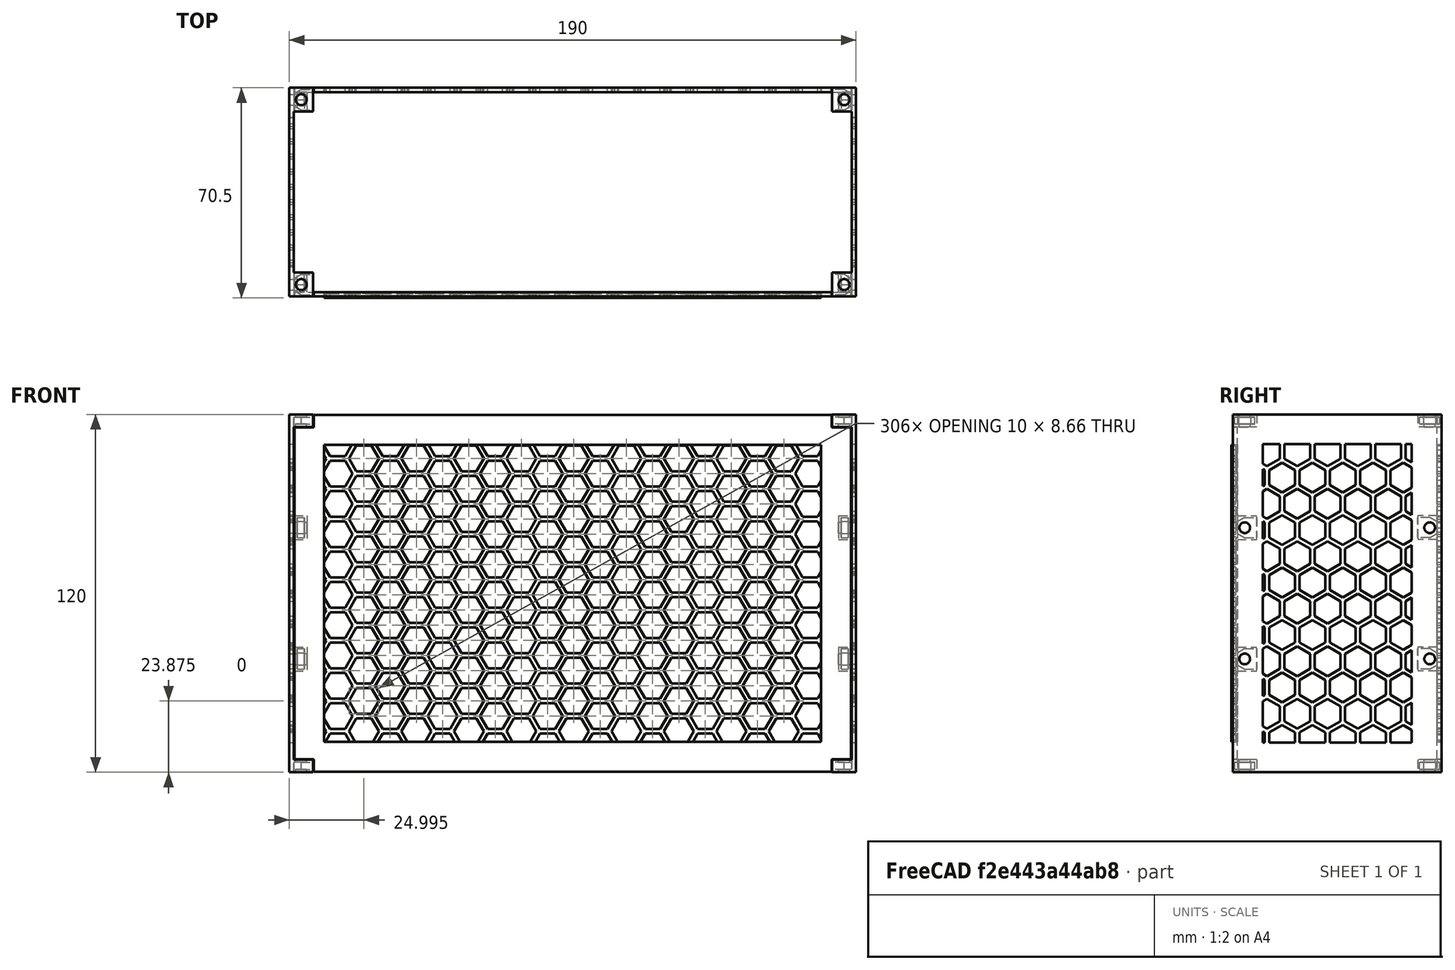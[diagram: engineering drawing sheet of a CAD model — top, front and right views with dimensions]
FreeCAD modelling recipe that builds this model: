
FCSTD DOCUMENT  (FreeCAD 0.18R4 (GitTag))
Label: tapasV3
License: CreativeCommons Attribution-ShareAlike
LicenseURL: http://creativecommons.org/licenses/by-sa/4.0/
objects: Part::Box×68, Part::Cut×60, Part::MultiFuse×46, Part::Cylinder×24, Part::Prism×16, Part::Feature×8
note: 222 computed .brp shape members not serialized (recipe doc carries the construction recipe); baked Part::Feature solids carry a one-line shape summary decoded from their .brp

FEATURE [Part::Feature] Cut001001001002003001008002002033001001001001001001001002001001002001045002003017008007002010007002014003017100  label="panal_simple_5_1.007"
  Placement = pos=(-89.5,0,0) rot=(0,1,0;1.5708rad)
  shape: bbox 1 x 260 x 260 mm, 5734 faces, 649 solids (baked)
FEATURE [Part::Feature] Cut001001001002003001008002002033001001001001001001001002001001002001045002003017008007002010007002014003017101  label="panal_simple_5_1.008"
  Placement = pos=(-88.5,0,0) rot=(0,1,0;1.5708rad)
  shape: bbox 1 x 260 x 260 mm, 5734 faces, 649 solids (baked)
FEATURE [Part::Feature] Cut001001001002003001008002002033001001001001001001001002001001002001045002003017008007002010007002014003017142  label="panal_simple_5_1.012"
  Placement = pos=(-113,18.7,0) rot=(-1,0,0;1.5708rad)
  shape: bbox 260 x 1 x 260 mm, 5734 faces, 649 solids (baked)
FEATURE [Part::Feature] Cut001001001002003001008002002033001001001001001001001002001001002001045002003017008007002010007002014003017075  label="panal_simple_5_1.006"
  Placement = pos=(-89.5,0,0) rot=(0,1,0;1.5708rad)
  shape: bbox 1 x 260 x 260 mm, 5734 faces, 649 solids (baked)
FEATURE [Part::Feature] Cut001001001002003001008002002033001001001001001001001002001001002001045002003017008007002010007002014003017148  label="panal_simple_5_1.013"
  Placement = pos=(-113,18.7,0) rot=(-1,0,0;1.5708rad)
  shape: bbox 260 x 1 x 260 mm, 5734 faces, 649 solids (baked)
FEATURE [Part::Feature] Cut001001001002003001008002002033001001001001001001001002001001002001045002003017008007002010007002014003017149  label="panal_simple_5_1.014"
  Placement = pos=(-113,17.8,0) rot=(-1,0,0;1.5708rad)
  shape: bbox 260 x 1 x 260 mm, 5734 faces, 649 solids (baked)
FEATURE [Part::Feature] Cut001004  label="panal_simple_5_1.5"
  Placement = pos=(-88.5,0,0) rot=(0,1,0;1.5708rad)
  shape: bbox 1 x 260 x 260 mm, 5734 faces, 649 solids (baked)
FEATURE [Part::Feature] Cut001001001002003001008002002033001001001001001001001002001001002001045002003017008007002010007002014003017141  label="panal_simple_5_1.011"
  Placement = pos=(-113,17.8,0) rot=(-1,0,0;1.5708rad)
  shape: bbox 260 x 1 x 260 mm, 5734 faces, 649 solids (baked)
FEATURE [Part::Box] Box089  label="Cube063"
  AttacherType = Attacher::AttachEngine3D
  Height = 4.2
  Length = 1
  Placement = pos=(-89,19,-111.2) rot=(0,0,1;0rad)
  Width = 8
FEATURE [Part::Box] Box079  label="Cube053"
  AttacherType = Attacher::AttachEngine3D
  Height = 100
  Length = 1.5
  Placement = pos=(-89,29,-217) rot=(0,0,1;0rad)
  Width = 50
FEATURE [Part::Box] Box077  label="Cube051"
  AttacherType = Attacher::AttachEngine3D
  Height = 120
  Length = 1.5
  Placement = pos=(-89,19,-227) rot=(0,0,1;0rad)
  Width = 70
FEATURE [Part::Cylinder] Cylinder037
  Angle = 360
  AttacherType = Attacher::AttachEngine3D
  Height = 10
  Placement = pos=(-91,85,-145) rot=(0.57735,0.57735,0.57735;2.0944rad)
  Radius = 1.8
FEATURE [Part::Cylinder] Cylinder035
  Angle = 360
  AttacherType = Attacher::AttachEngine3D
  Height = 10
  Placement = pos=(-91,23,-145) rot=(0.57735,0.57735,0.57735;2.0944rad)
  Radius = 1.8
FEATURE [Part::Cylinder] Cylinder038
  Angle = 360
  AttacherType = Attacher::AttachEngine3D
  Height = 10
  Placement = pos=(-91,85,-189) rot=(0.57735,0.57735,0.57735;2.0944rad)
  Radius = 1.8
FEATURE [Part::Box] Box078  label="Cube052"
  AttacherType = Attacher::AttachEngine3D
  Height = 100
  Length = 1.5
  Placement = pos=(-89,29,-217) rot=(0,0,1;0rad)
  Width = 50
FEATURE [Part::Cut] Cut001001001002003001008002002033001001001001001001001002001001002001045002003017008007002010007002014003017076
  Base = -> Box078
  Tool = -> Cut001004
FEATURE [Part::Cut] Cut001001001002003001008002002033001001001001001001001002001001002001045002003017008007002010007002014003017077  label="panal1"
  Base = -> Cut001001001002003001008002002033001001001001001001001002001001002001045002003017008007002010007002014003017076
  Tool = -> Cut001001001002003001008002002033001001001001001001001002001001002001045002003017008007002010007002014003017075
FEATURE [Part::Cylinder] Cylinder036
  Angle = 360
  AttacherType = Attacher::AttachEngine3D
  Height = 10
  Placement = pos=(-91,23,-189) rot=(0.57735,0.57735,0.57735;2.0944rad)
  Radius = 1.8
FEATURE [Part::Box] Box124  label="Cube098"
  AttacherType = Attacher::AttachEngine3D
  Height = 4.2
  Length = 1
  Placement = pos=(-89,19,-111.2) rot=(0,0,1;0rad)
  Width = 8
FEATURE [Part::Cylinder] Cylinder055
  Angle = 360
  AttacherType = Attacher::AttachEngine3D
  Height = 10
  Placement = pos=(-85,23,-112) rot=(0,0,1;0rad)
  Radius = 1.85
FEATURE [Part::Cylinder] Cylinder041
  Angle = 360
  AttacherType = Attacher::AttachEngine3D
  Height = 10
  Placement = pos=(-85,23,-112) rot=(0,0,1;0rad)
  Radius = 1.85
FEATURE [Part::Box] Box090  label="Cube064"
  AttacherType = Attacher::AttachEngine3D
  Height = 4.2
  Length = 7
  Placement = pos=(-88,19,-111.2) rot=(0,0,1;0rad)
  Width = 8
FEATURE [Part::Box] Box122  label="Cube096"
  AttacherType = Attacher::AttachEngine3D
  Height = 4.2
  Length = 1
  Placement = pos=(-89,19,-111.2) rot=(0,0,1;0rad)
  Width = 8
FEATURE [Part::Box] Box123  label="Cube097"
  AttacherType = Attacher::AttachEngine3D
  Height = 4.2
  Length = 7
  Placement = pos=(-88,19,-111.2) rot=(0,0,1;0rad)
  Width = 8
FEATURE [Part::Cut] Cut001001001002003001008002002033001001001001001001001002001001002001045002003017008007002010007002014003017118
  Base = -> Box123
  Tool = -> Cylinder055
FEATURE [Part::Box] Box088  label="Cube062"
  AttacherType = Attacher::AttachEngine3D
  Height = 2.4
  Length = 24
  Placement = pos=(-85,19.6,-110.2) rot=(0,0,1;0rad)
  Width = 6.8
FEATURE [Part::Prism] Prism014
  AttacherType = Attacher::AttachEngine3D
  Circumradius = 3.4
  Height = 2.4
  Placement = pos=(-85,23,-110.2) rot=(0,0,1;0.523599rad)
  Polygon = 6
FEATURE [Part::Prism] Prism013
  AttacherType = Attacher::AttachEngine3D
  Circumradius = 3.4
  Height = 2.4
  Placement = pos=(-85,23,-110.2) rot=(0,0,1;0.523599rad)
  Polygon = 6
FEATURE [Part::Box] Box086  label="Cube060"
  AttacherType = Attacher::AttachEngine3D
  Height = 4.2
  Length = 1
  Placement = pos=(-89,19,-111.2) rot=(0,0,1;0rad)
  Width = 8
FEATURE [Part::Prism] Prism015
  AttacherType = Attacher::AttachEngine3D
  Circumradius = 3.4
  Height = 2.4
  Placement = pos=(-85,23,-110.2) rot=(0,0,1;0.523599rad)
  Polygon = 6
FEATURE [Part::Box] Box087  label="Cube061"
  AttacherType = Attacher::AttachEngine3D
  Height = 4.2
  Length = 7
  Placement = pos=(-88,19,-111.2) rot=(0,0,1;0rad)
  Width = 8
FEATURE [Part::Cylinder] Cylinder039
  Angle = 360
  AttacherType = Attacher::AttachEngine3D
  Height = 10
  Placement = pos=(-85,23,-112) rot=(0,0,1;0rad)
  Radius = 1.85
FEATURE [Part::Box] Box085  label="Cube059"
  AttacherType = Attacher::AttachEngine3D
  Height = 2.4
  Length = 24
  Placement = pos=(-85,19.6,-110.2) rot=(0,0,1;0rad)
  Width = 6.8
FEATURE [Part::MultiFuse] Fusion007002009027003005008003003006005017002002002002002002002032016
  Placement = pos=(0,0,-0.1) rot=(0,0,1;0rad)
  Shapes = -> [Prism014,Box085]
FEATURE [Part::Box] Box082  label="Cube056"
  AttacherType = Attacher::AttachEngine3D
  Height = 2.4
  Length = 24
  Placement = pos=(-85,19.6,-110.2) rot=(0,0,1;0rad)
  Width = 6.8
FEATURE [Part::MultiFuse] Fusion007002009027003005008003003006005017002002002002002002002032014
  Placement = pos=(0,0,-0.1) rot=(0,0,1;0rad)
  Shapes = -> [Prism013,Box082]
FEATURE [Part::Box] Box083  label="Cube057"
  AttacherType = Attacher::AttachEngine3D
  Height = 4.2
  Length = 1
  Placement = pos=(-89,19,-111.2) rot=(0,0,1;0rad)
  Width = 8
FEATURE [Part::Box] Box084  label="Cube058"
  AttacherType = Attacher::AttachEngine3D
  Height = 4.2
  Length = 7
  Placement = pos=(-88,19,-111.2) rot=(0,0,1;0rad)
  Width = 8
FEATURE [Part::Cut] Cut001001001002003001008002002033001001001001001001001002001001002001045002003017008007002010007002014003017085
  Base = -> Box084
  Tool = -> Cylinder039
FEATURE [Part::MultiFuse] Fusion007002009027003005008003003006005017002002002002002002002032015
  Shapes = -> [Box083,Cut001001001002003001008002002033001001001001001001001002001001002001045002003017008007002010007002014003017085]
FEATURE [Part::Cut] Cut001001001002003001008002002033001001001001001001001002001001002001045002003017008007002010007002014003017084  label="pocket_v010"
  Base = -> Fusion007002009027003005008003003006005017002002002002002002002032015
  Tool = -> Fusion007002009027003005008003003006005017002002002002002002002032014
FEATURE [Part::Cylinder] Cylinder040
  Angle = 360
  AttacherType = Attacher::AttachEngine3D
  Height = 10
  Placement = pos=(-85,23,-112) rot=(0,0,1;0rad)
  Radius = 1.85
FEATURE [Part::Cut] Cut001001001002003001008002002033001001001001001001001002001001002001045002003017008007002010007002014003017087
  Base = -> Box087
  Tool = -> Cylinder040
FEATURE [Part::Box] Box104  label="Cube078"
  AttacherType = Attacher::AttachEngine3D
  Height = 4.2
  Length = 1
  Placement = pos=(-89,19,-111.2) rot=(0,0,1;0rad)
  Width = 8
FEATURE [Part::Box] Box125  label="Cube099"
  AttacherType = Attacher::AttachEngine3D
  Height = 4.2
  Length = 7
  Placement = pos=(-88,19,-111.2) rot=(0,0,1;0rad)
  Width = 8
FEATURE [Part::Box] Box121  label="Cube095"
  AttacherType = Attacher::AttachEngine3D
  Height = 2.4
  Length = 24
  Placement = pos=(-85,19.6,-110.2) rot=(0,0,1;0rad)
  Width = 6.8
FEATURE [Part::Box] Box112  label="Cube086"
  AttacherType = Attacher::AttachEngine3D
  Height = 4.2
  Length = 1
  Placement = pos=(-89,19,-111.2) rot=(0,0,1;0rad)
  Width = 8
FEATURE [Part::Box] Box111  label="Cube085"
  AttacherType = Attacher::AttachEngine3D
  Height = 2.4
  Length = 24
  Placement = pos=(-85,19.6,-110.2) rot=(0,0,1;0rad)
  Width = 6.8
FEATURE [Part::Cylinder] Cylinder052
  Angle = 360
  AttacherType = Attacher::AttachEngine3D
  Height = 10
  Placement = pos=(-85,23,-112) rot=(0,0,1;0rad)
  Radius = 1.85
FEATURE [Part::Box] Box117  label="Cube091"
  AttacherType = Attacher::AttachEngine3D
  Height = 4.2
  Length = 7
  Placement = pos=(-88,19,-111.2) rot=(0,0,1;0rad)
  Width = 8
FEATURE [Part::Cylinder] Cylinder048
  Angle = 360
  AttacherType = Attacher::AttachEngine3D
  Height = 10
  Placement = pos=(-91,23,-145) rot=(0.57735,0.57735,0.57735;2.0944rad)
  Radius = 1.8
FEATURE [Part::Cylinder] Cylinder050
  Angle = 360
  AttacherType = Attacher::AttachEngine3D
  Height = 10
  Placement = pos=(-91,23,-189) rot=(0.57735,0.57735,0.57735;2.0944rad)
  Radius = 1.8
FEATURE [Part::Cylinder] Cylinder054
  Angle = 360
  AttacherType = Attacher::AttachEngine3D
  Height = 10
  Placement = pos=(-85,23,-112) rot=(0,0,1;0rad)
  Radius = 1.85
FEATURE [Part::Prism] Prism023
  AttacherType = Attacher::AttachEngine3D
  Circumradius = 3.4
  Height = 2.4
  Placement = pos=(-85,23,-110.2) rot=(0,0,1;0.523599rad)
  Polygon = 6
FEATURE [Part::Cylinder] Cylinder053
  Angle = 360
  AttacherType = Attacher::AttachEngine3D
  Height = 10
  Placement = pos=(-85,23,-112) rot=(0,0,1;0rad)
  Radius = 1.85
FEATURE [Part::Prism] Prism025
  AttacherType = Attacher::AttachEngine3D
  Circumradius = 3.4
  Height = 2.4
  Placement = pos=(-85,23,-110.2) rot=(0,0,1;0.523599rad)
  Polygon = 6
FEATURE [Part::Box] Box115  label="Cube089"
  AttacherType = Attacher::AttachEngine3D
  Height = 2.4
  Length = 24
  Placement = pos=(-85,19.6,-110.2) rot=(0,0,1;0rad)
  Width = 6.8
FEATURE [Part::Box] Box113  label="Cube087"
  AttacherType = Attacher::AttachEngine3D
  Height = 4.2
  Length = 7
  Placement = pos=(-88,19,-111.2) rot=(0,0,1;0rad)
  Width = 8
FEATURE [Part::Cut] Cut001001001002003001008002002033001001001001001001001002001001002001045002003017008007002010007002014003017107
  Base = -> Box113
  Tool = -> Cylinder053
FEATURE [Part::Box] Box116  label="Cube090"
  AttacherType = Attacher::AttachEngine3D
  Height = 4.2
  Length = 1
  Placement = pos=(-89,19,-111.2) rot=(0,0,1;0rad)
  Width = 8
FEATURE [Part::Box] Box109  label="Cube083"
  AttacherType = Attacher::AttachEngine3D
  Height = 100
  Length = 1.5
  Placement = pos=(-89,29,-217) rot=(0,0,1;0rad)
  Width = 50
FEATURE [Part::Cut] Cut001001001002003001008002002033001001001001001001001002001001002001045002003017008007002010007002014003017111
  Base = -> Box109
  Tool = -> Cut001001001002003001008002002033001001001001001001001002001001002001045002003017008007002010007002014003017101
FEATURE [Part::Cylinder] Cylinder049
  Angle = 360
  AttacherType = Attacher::AttachEngine3D
  Height = 10
  Placement = pos=(-91,85,-189) rot=(0.57735,0.57735,0.57735;2.0944rad)
  Radius = 1.8
FEATURE [Part::Cylinder] Cylinder051
  Angle = 360
  AttacherType = Attacher::AttachEngine3D
  Height = 10
  Placement = pos=(-85,23,-112) rot=(0,0,1;0rad)
  Radius = 1.85
FEATURE [Part::Prism] Prism021
  AttacherType = Attacher::AttachEngine3D
  Circumradius = 3.4
  Height = 2.4
  Placement = pos=(-85,23,-110.2) rot=(0,0,1;0.523599rad)
  Polygon = 6
FEATURE [Part::Prism] Prism022
  AttacherType = Attacher::AttachEngine3D
  Circumradius = 3.4
  Height = 2.4
  Placement = pos=(-85,23,-110.2) rot=(0,0,1;0.523599rad)
  Polygon = 6
FEATURE [Part::Box] Box114  label="Cube088"
  AttacherType = Attacher::AttachEngine3D
  Height = 2.4
  Length = 24
  Placement = pos=(-85,19.6,-110.2) rot=(0,0,1;0rad)
  Width = 6.8
FEATURE [Part::Box] Box110  label="Cube084"
  AttacherType = Attacher::AttachEngine3D
  Height = 4.2
  Length = 7
  Placement = pos=(-88,19,-111.2) rot=(0,0,1;0rad)
  Width = 8
FEATURE [Part::Cut] Cut001001001002003001008002002033001001001001001001001002001001002001045002003017008007002010007002014003017114
  Base = -> Box110
  Tool = -> Cylinder051
FEATURE [Part::Box] Box118  label="Cube092"
  AttacherType = Attacher::AttachEngine3D
  Height = 4.2
  Length = 1
  Placement = pos=(-89,19,-111.2) rot=(0,0,1;0rad)
  Width = 8
FEATURE [Part::Prism] Prism024
  AttacherType = Attacher::AttachEngine3D
  Circumradius = 3.4
  Height = 2.4
  Placement = pos=(-85,23,-110.2) rot=(0,0,1;0.523599rad)
  Polygon = 6
FEATURE [Part::Box] Box119  label="Cube093"
  AttacherType = Attacher::AttachEngine3D
  Height = 2.4
  Length = 24
  Placement = pos=(-85,19.6,-110.2) rot=(0,0,1;0rad)
  Width = 6.8
FEATURE [Part::Box] Box120  label="Cube094"
  AttacherType = Attacher::AttachEngine3D
  Height = 4.2
  Length = 7
  Placement = pos=(-88,19,-111.2) rot=(0,0,1;0rad)
  Width = 8
FEATURE [Part::Cut] Cut001001001002003001008002002033001001001001001001001002001001002001045002003017008007002010007002014003017115
  Base = -> Box120
  Tool = -> Cylinder054
FEATURE [Part::MultiFuse] Fusion007002009027003005008003003006005017002002002002002002002032036
  Shapes = -> [Box118,Cut001001001002003001008002002033001001001001001001001002001001002001045002003017008007002010007002014003017115]
FEATURE [Part::MultiFuse] Fusion007002009027003005008003003006005017002002002002002002002032018
  Placement = pos=(0,0,-0.1) rot=(0,0,1;0rad)
  Shapes = -> [Prism015,Box088]
FEATURE [Part::MultiFuse] Fusion007002009027003005008003003006005017002002002002002002002032034
  Placement = pos=(0,0,-0.1) rot=(0,0,1;0rad)
  Shapes = -> [Prism021,Box114]
FEATURE [Part::MultiFuse] Fusion007002009027003005008003003006005017002002002002002002002032017
  Shapes = -> [Box086,Cut001001001002003001008002002033001001001001001001001002001001002001045002003017008007002010007002014003017087]
FEATURE [Part::Cut] Cut001001001002003001008002002033001001001001001001001002001001002001045002003017008007002010007002014003017086  label="pocket_v011"
  Base = -> Fusion007002009027003005008003003006005017002002002002002002002032017
  Placement = pos=(0,0,-115.8) rot=(0,0,1;0rad)
  Tool = -> Fusion007002009027003005008003003006005017002002002002002002002032016
FEATURE [Part::MultiFuse] Fusion007002009027003005008003003006005017002002002002002002002032035
  Placement = pos=(0,0,-0.1) rot=(0,0,1;0rad)
  Shapes = -> [Prism023,Box111]
FEATURE [Part::MultiFuse] Fusion007002009027003005008003003006005017002002002002002002002032032
  Placement = pos=(0,0,-0.1) rot=(0,0,1;0rad)
  Shapes = -> [Prism022,Box115]
FEATURE [Part::Cut] Cut001001001002003001008002002033001001001001001001001002001001002001045002003017008007002010007002014003017089
  Base = -> Box090
  Tool = -> Cylinder041
FEATURE [Part::MultiFuse] Fusion007002009027003005008003003006005017002002002002002002002032019
  Shapes = -> [Box089,Cut001001001002003001008002002033001001001001001001001002001001002001045002003017008007002010007002014003017089]
FEATURE [Part::Cut] Cut001001001002003001008002002033001001001001001001001002001001002001045002003017008007002010007002014003017088  label="pocket_v012"
  Base = -> Fusion007002009027003005008003003006005017002002002002002002002032019
  Placement = pos=(0,62,0) rot=(0,0,1;0rad)
  Tool = -> Fusion007002009027003005008003003006005017002002002002002002002032018
FEATURE [Part::Cylinder] Cylinder056
  Angle = 360
  AttacherType = Attacher::AttachEngine3D
  Height = 10
  Placement = pos=(-85,23,-112) rot=(0,0,1;0rad)
  Radius = 1.85
FEATURE [Part::Cut] Cut001001001002003001008002002033001001001001001001001002001001002001045002003017008007002010007002014003017119
  Base = -> Box125
  Tool = -> Cylinder056
FEATURE [Part::Prism] Prism020
  AttacherType = Attacher::AttachEngine3D
  Circumradius = 3.4
  Height = 2.4
  Placement = pos=(-85,23,-110.2) rot=(0,0,1;0.523599rad)
  Polygon = 6
FEATURE [Part::Cylinder] Cylinder047
  Angle = 360
  AttacherType = Attacher::AttachEngine3D
  Height = 10
  Placement = pos=(-91,85,-145) rot=(0.57735,0.57735,0.57735;2.0944rad)
  Radius = 1.8
FEATURE [Part::Box] Box103  label="Cube077"
  AttacherType = Attacher::AttachEngine3D
  Height = 2.4
  Length = 24
  Placement = pos=(-85,19.6,-110.2) rot=(0,0,1;0rad)
  Width = 6.8
FEATURE [Part::MultiFuse] Fusion007002009027003005008003003006005017002002002002002002002032028
  Placement = pos=(0,0,-0.1) rot=(0,0,1;0rad)
  Shapes = -> [Prism020,Box103]
FEATURE [Part::Box] Box106  label="Cube080"
  AttacherType = Attacher::AttachEngine3D
  Height = 4.2
  Length = 1
  Placement = pos=(-89,19,-111.2) rot=(0,0,1;0rad)
  Width = 8
FEATURE [Part::Cylinder] Cylinder046
  Angle = 360
  AttacherType = Attacher::AttachEngine3D
  Height = 10
  Placement = pos=(-85,23,-112) rot=(0,0,1;0rad)
  Radius = 1.85
FEATURE [Part::Box] Box107  label="Cube081"
  AttacherType = Attacher::AttachEngine3D
  Height = 100
  Length = 1.5
  Placement = pos=(-89,29,-217) rot=(0,0,1;0rad)
  Width = 50
FEATURE [Part::Box] Box108  label="Cube082"
  AttacherType = Attacher::AttachEngine3D
  Height = 120
  Length = 1.5
  Placement = pos=(-89,19,-227) rot=(0,0,1;0rad)
  Width = 70
FEATURE [Part::Box] Box105  label="Cube079"
  AttacherType = Attacher::AttachEngine3D
  Height = 4.2
  Length = 7
  Placement = pos=(-88,19,-111.2) rot=(0,0,1;0rad)
  Width = 8
FEATURE [Part::Cut] Cut001001001002003001008002002033001001001001001001001002001001002001045002003017008007002010007002014003017099
  Base = -> Box105
  Tool = -> Cylinder046
FEATURE [Part::MultiFuse] Fusion007002009027003005008003003006005017002002002002002002002032029
  Shapes = -> [Box104,Cut001001001002003001008002002033001001001001001001001002001001002001045002003017008007002010007002014003017099]
FEATURE [Part::Cut] Cut001001001002003001008002002033001001001001001001001002001001002001045002003017008007002010007002014003017098  label="pocket_v017"
  Base = -> Fusion007002009027003005008003003006005017002002002002002002002032029
  Placement = pos=(0,62,-115.8) rot=(0,0,1;0rad)
  Tool = -> Fusion007002009027003005008003003006005017002002002002002002002032028
FEATURE [Part::MultiFuse] Fusion007002009027003005008003003006005017002002002002002002002032006  label="lateral_izquierdo_v2_001"
  Shapes = -> [Box077,Cut001001001002003001008002002033001001001001001001001002001001002001045002003017008007002010007002014003017088,Cut001001001002003001008002002033001001001001001001001002001001002001045002003017008007002010007002014003017084,Cut001001001002003001008002002033001001001001001001001002001001002001045002003017008007002010007002014003017086,+1 more]
FEATURE [Part::Cut] Cut001001001002003001008002002033001001001001001001001002001001002001045002003017008007002010007002014003017078
  Base = -> Fusion007002009027003005008003003006005017002002002002002002002032006
  Tool = -> Box079
FEATURE [Part::MultiFuse] Fusion007002009027003005008003003006005017002002002002002002002032007  label="lateral_izquierdo_v2_00101"
  Shapes = -> [Cut001001001002003001008002002033001001001001001001001002001001002001045002003017008007002010007002014003017078,Cut001001001002003001008002002033001001001001001001001002001001002001045002003017008007002010007002014003017077]
FEATURE [Part::Cut] Cut001001001002003001008002002033001001001001001001001002001001002001045002003017008007002010007002014003017079
  Base = -> Fusion007002009027003005008003003006005017002002002002002002002032007
  Tool = -> Cylinder035
FEATURE [Part::Cut] Cut001001001002003001008002002033001001001001001001001002001001002001045002003017008007002010007002014003017080
  Base = -> Cut001001001002003001008002002033001001001001001001001002001001002001045002003017008007002010007002014003017079
  Tool = -> Cylinder036
FEATURE [Part::Cut] Cut001001001002003001008002002033001001001001001001001002001001002001045002003017008007002010007002014003017081
  Base = -> Cut001001001002003001008002002033001001001001001001001002001001002001045002003017008007002010007002014003017080
  Tool = -> Cylinder038
FEATURE [Part::Cut] Cut001001001002003001008002002033001001001001001001001002001001002001045002003017008007002010007002014003017082  label="lateral_izquierdo_v3"
  Base = -> Cut001001001002003001008002002033001001001001001001001002001001002001045002003017008007002010007002014003017081
  Tool = -> Cylinder037
FEATURE [Part::Cut] Cut001001001002003001008002002033001001001001001001001002001001002001045002003017008007002010007002014003017105
  Base = -> Box117
  Tool = -> Cylinder052
FEATURE [Part::MultiFuse] Fusion007002009027003005008003003006005017002002002002002002002032033
  Shapes = -> [Box116,Cut001001001002003001008002002033001001001001001001001002001001002001045002003017008007002010007002014003017105]
FEATURE [Part::Cut] Cut001001001002003001008002002033001001001001001001001002001001002001045002003017008007002010007002014003017104  label="pocket_v018"
  Base = -> Fusion007002009027003005008003003006005017002002002002002002002032033
  Placement = pos=(-176.5,46,0) rot=(0,0,1;3.14159rad)
  Tool = -> Fusion007002009027003005008003003006005017002002002002002002002032032
FEATURE [Part::Cut] Cut001001001002003001008002002033001001001001001001001002001001002001045002003017008007002010007002014003017103  label="panal002"
  Base = -> Cut001001001002003001008002002033001001001001001001001002001001002001045002003017008007002010007002014003017111
  Tool = -> Cut001001001002003001008002002033001001001001001001001002001001002001045002003017008007002010007002014003017100
FEATURE [Part::MultiFuse] Fusion007002009027003005008003003006005017002002002002002002002032038
  Shapes = -> [Box112,Cut001001001002003001008002002033001001001001001001001002001001002001045002003017008007002010007002014003017107]
FEATURE [Part::Cut] Cut001001001002003001008002002033001001001001001001001002001001002001045002003017008007002010007002014003017106  label="pocket_v019"
  Base = -> Fusion007002009027003005008003003006005017002002002002002002002032038
  Placement = pos=(-176.5,46,-115.8) rot=(0,0,1;3.14159rad)
  Tool = -> Fusion007002009027003005008003003006005017002002002002002002002032034
FEATURE [Part::MultiFuse] Fusion007002009027003005008003003006005017002002002002002002002032040
  Placement = pos=(0,0,-0.1) rot=(0,0,1;0rad)
  Shapes = -> [Prism025,Box121]
FEATURE [Part::MultiFuse] Fusion007002009027003005008003003006005017002002002002002002002032041
  Shapes = -> [Box122,Cut001001001002003001008002002033001001001001001001001002001001002001045002003017008007002010007002014003017118]
FEATURE [Part::Cut] Cut001001001002003001008002002033001001001001001001001002001001002001045002003017008007002010007002014003017117  label="pocket_v022"
  Base = -> Fusion007002009027003005008003003006005017002002002002002002002032041
  Placement = pos=(23.9,108,-168) rot=(0.57735,0.57735,0.57735;2.0944rad)
  Tool = -> Fusion007002009027003005008003003006005017002002002002002002002032040
FEATURE [Part::MultiFuse] Fusion007002009027003005008003003006005017002002002002002002002032037
  Shapes = -> [Box106,Cut001001001002003001008002002033001001001001001001001002001001002001045002003017008007002010007002014003017114]
FEATURE [Part::Cut] Cut001001001002003001008002002033001001001001001001001002001001002001045002003017008007002010007002014003017113  label="pocket_v020"
  Base = -> Fusion007002009027003005008003003006005017002002002002002002002032037
  Placement = pos=(-176.5,108,0) rot=(0,0,1;3.14159rad)
  Tool = -> Fusion007002009027003005008003003006005017002002002002002002002032035
FEATURE [Part::MultiFuse] Fusion007002009027003005008003003006005017002002002002002002002032039
  Placement = pos=(0,0,-0.1) rot=(0,0,1;0rad)
  Shapes = -> [Prism024,Box119]
FEATURE [Part::Cut] Cut001001001002003001008002002033001001001001001001001002001001002001045002003017008007002010007002014003017116  label="pocket_v021"
  Base = -> Fusion007002009027003005008003003006005017002002002002002002002032036
  Placement = pos=(-176.5,108,-115.8) rot=(0,0,1;3.14159rad)
  Tool = -> Fusion007002009027003005008003003006005017002002002002002002002032039
FEATURE [Part::MultiFuse] Fusion007002009027003005008003003006005017002002002002002002002032030  label="lateral_izquierdo_v2_00102"
  Shapes = -> [Box108,Cut001001001002003001008002002033001001001001001001001002001001002001045002003017008007002010007002014003017113,Cut001001001002003001008002002033001001001001001001001002001001002001045002003017008007002010007002014003017104,Cut001001001002003001008002002033001001001001001001001002001001002001045002003017008007002010007002014003017106,+1 more]
FEATURE [Part::Cut] Cut001001001002003001008002002033001001001001001001001002001001002001045002003017008007002010007002014003017108
  Base = -> Fusion007002009027003005008003003006005017002002002002002002002032030
  Tool = -> Box107
FEATURE [Part::MultiFuse] Fusion007002009027003005008003003006005017002002002002002002002032031  label="lateral_izquierdo_v2_00103"
  Shapes = -> [Cut001001001002003001008002002033001001001001001001001002001001002001045002003017008007002010007002014003017108,Cut001001001002003001008002002033001001001001001001001002001001002001045002003017008007002010007002014003017103]
FEATURE [Part::Cut] Cut001001001002003001008002002033001001001001001001001002001001002001045002003017008007002010007002014003017110
  Base = -> Fusion007002009027003005008003003006005017002002002002002002002032031
  Tool = -> Cylinder048
FEATURE [Part::Cut] Cut001001001002003001008002002033001001001001001001001002001001002001045002003017008007002010007002014003017109
  Base = -> Cut001001001002003001008002002033001001001001001001001002001001002001045002003017008007002010007002014003017110
  Tool = -> Cylinder050
FEATURE [Part::Cut] Cut001001001002003001008002002033001001001001001001001002001001002001045002003017008007002010007002014003017112
  Base = -> Cut001001001002003001008002002033001001001001001001001002001001002001045002003017008007002010007002014003017109
  Tool = -> Cylinder049
FEATURE [Part::Cut] Cut001001001002003001008002002033001001001001001001001002001001002001045002003017008007002010007002014003017102  label="lateral_derecho_v3"
  Base = -> Cut001001001002003001008002002033001001001001001001001002001001002001045002003017008007002010007002014003017112
  Placement = pos=(188.5,0,0) rot=(0,0,1;0rad)
  Tool = -> Cylinder047
FEATURE [Part::MultiFuse] Fusion007002009027003005008003003006005017002002002002002002002032043
  Shapes = -> [Box124,Cut001001001002003001008002002033001001001001001001001002001001002001045002003017008007002010007002014003017119]
FEATURE [Part::Box] Box156  label="Cube124"
  AttacherType = Attacher::AttachEngine3D
  Height = 4.4
  Length = 6.7
  Placement = pos=(92.8,17,-227) rot=(0,0,1;0rad)
  Width = 10
FEATURE [Part::Box] Box157  label="Cube125"
  AttacherType = Attacher::AttachEngine3D
  Height = 4.4
  Length = 6.7
  Placement = pos=(92.8,17,-111.4) rot=(0,0,1;0rad)
  Width = 10
FEATURE [Part::Box] Box152  label="base_tapa003"
  AttacherType = Attacher::AttachEngine3D
  Height = 99.6
  Length = 166.6
  Placement = pos=(-77.3,18.5,-216.8) rot=(0,0,1;0rad)
  Width = 1.5
FEATURE [Part::Cut] Cut001001001002003001008002002033001001001001001001001002001001002001045002003017008007002010007002014003017143
  Base = -> Box152
  Tool = -> Cut001001001002003001008002002033001001001001001001001002001001002001045002003017008007002010007002014003017142
FEATURE [Part::Cut] Cut001001001002003001008002002033001001001001001001001002001001002001045002003017008007002010007002014003017144  label="enrejillado_base_o_tapa"
  Base = -> Cut001001001002003001008002002033001001001001001001001002001001002001045002003017008007002010007002014003017143
  Placement = pos=(0,69,0) rot=(0,0,1;0rad)
  Tool = -> Cut001001001002003001008002002033001001001001001001001002001001002001045002003017008007002010007002014003017141
FEATURE [Part::Box] Box150  label="corta_enrejilaldo_base_tapa001"
  AttacherType = Attacher::AttachEngine3D
  Height = 99.6
  Length = 166.6
  Placement = pos=(-77.3,18.5,-216.8) rot=(0,0,1;0rad)
  Width = 3
FEATURE [Part::Box] Box153  label="base_tapa004"
  AttacherType = Attacher::AttachEngine3D
  Height = 99.6
  Length = 166.6
  Placement = pos=(-77.3,86.5,-216.8) rot=(0,0,1;0rad)
  Width = 3
FEATURE [Part::Box] Box154  label="base_tapa005"
  AttacherType = Attacher::AttachEngine3D
  Height = 99.6
  Length = 166.6
  Placement = pos=(-77.3,18.5,-216.8) rot=(0,0,1;0rad)
  Width = 1.5
FEATURE [Part::Cut] Cut001001001002003001008002002033001001001001001001001002001001002001045002003017008007002010007002014003017147
  Base = -> Box154
  Tool = -> Cut001001001002003001008002002033001001001001001001001002001001002001045002003017008007002010007002014003017148
FEATURE [Part::Cut] Cut001001001002003001008002002033001001001001001001001002001001002001045002003017008007002010007002014003017155
  Base = -> Cut001001001002003001008002002033001001001001001001001002001001002001045002003017008007002010007002014003017147
  Tool = -> Cut001001001002003001008002002033001001001001001001001002001001002001045002003017008007002010007002014003017149
FEATURE [Part::Box] Box149  label="Cube122"
  AttacherType = Attacher::AttachEngine3D
  Height = 4.4
  Length = 6.7
  Placement = pos=(-87.5,17,-111.4) rot=(0,0,1;0rad)
  Width = 10
FEATURE [Part::Box] Box155  label="Cube123"
  AttacherType = Attacher::AttachEngine3D
  Height = 4.4
  Length = 6.7
  Placement = pos=(-87.5,17,-111.4) rot=(0,0,1;0rad)
  Width = 10
FEATURE [Part::Box] Box158  label="Cube126"
  AttacherType = Attacher::AttachEngine3D
  Height = 4.4
  Length = 6.7
  Placement = pos=(-87.5,17,-227) rot=(0,0,1;0rad)
  Width = 10
FEATURE [Part::Box] Box159  label="base_tapa006"
  AttacherType = Attacher::AttachEngine3D
  Height = 119.6
  Length = 186.6
  Placement = pos=(-87.3,21,-226.8) rot=(0,0,1;0rad)
  Width = 1.5
FEATURE [Part::Box] Box147  label="Cube120"
  AttacherType = Attacher::AttachEngine3D
  Height = 4.4
  Length = 6.7
  Placement = pos=(92.8,17,-227) rot=(0,0,1;0rad)
  Width = 10
FEATURE [Part::Box] Box148  label="Cube121"
  AttacherType = Attacher::AttachEngine3D
  Height = 4.4
  Length = 6.7
  Placement = pos=(92.8,17,-111.4) rot=(0,0,1;0rad)
  Width = 10
FEATURE [Part::Box] Box146  label="Cube119"
  AttacherType = Attacher::AttachEngine3D
  Height = 4.4
  Length = 6.7
  Placement = pos=(-87.5,17,-227) rot=(0,0,1;0rad)
  Width = 10
FEATURE [Part::Cut] Cut001001001002003001008002002033001001001001001001001002001001002001045002003017008007002010007002014003017152
  Base = -> Box159
  Tool = -> Box158
FEATURE [Part::Cut] Cut001001001002003001008002002033001001001001001001001002001001002001045002003017008007002010007002014003017153
  Base = -> Cut001001001002003001008002002033001001001001001001001002001001002001045002003017008007002010007002014003017152
  Tool = -> Box155
FEATURE [Part::Cut] Cut001001001002003001008002002033001001001001001001001002001001002001045002003017008007002010007002014003017150
  Base = -> Cut001001001002003001008002002033001001001001001001001002001001002001045002003017008007002010007002014003017153
  Tool = -> Box157
FEATURE [Part::Cut] Cut001001001002003001008002002033001001001001001001001002001001002001045002003017008007002010007002014003017151  label="base_tapa_002"
  Base = -> Cut001001001002003001008002002033001001001001001001001002001001002001045002003017008007002010007002014003017150
  Placement = pos=(0,66.5,0) rot=(0,0,1;0rad)
  Tool = -> Box156
FEATURE [Part::Box] Box132  label="Cube106"
  AttacherType = Attacher::AttachEngine3D
  Height = 4.2
  Length = 1
  Placement = pos=(-89,19,-111.2) rot=(0,0,1;0rad)
  Width = 8
FEATURE [Part::Cylinder] Cylinder058
  Angle = 360
  AttacherType = Attacher::AttachEngine3D
  Height = 10
  Placement = pos=(-85,23,-112) rot=(0,0,1;0rad)
  Radius = 1.85
FEATURE [Part::Box] Box131  label="Cube105"
  AttacherType = Attacher::AttachEngine3D
  Height = 2.4
  Length = 24
  Placement = pos=(-85,19.6,-110.2) rot=(0,0,1;0rad)
  Width = 6.8
FEATURE [Part::Box] Box128  label="Cube102"
  AttacherType = Attacher::AttachEngine3D
  Height = 4.2
  Length = 7
  Placement = pos=(-88,19,-111.2) rot=(0,0,1;0rad)
  Width = 8
FEATURE [Part::Box] Box126  label="Cube100"
  AttacherType = Attacher::AttachEngine3D
  Height = 2.4
  Length = 24
  Placement = pos=(-85,19.6,-110.2) rot=(0,0,1;0rad)
  Width = 6.8
FEATURE [Part::Cylinder] Cylinder060
  Angle = 360
  AttacherType = Attacher::AttachEngine3D
  Height = 10
  Placement = pos=(-85,23,-112) rot=(0,0,1;0rad)
  Radius = 1.85
FEATURE [Part::Prism] Prism027
  AttacherType = Attacher::AttachEngine3D
  Circumradius = 3.4
  Height = 2.4
  Placement = pos=(-85,23,-110.2) rot=(0,0,1;0.523599rad)
  Polygon = 6
FEATURE [Part::Box] Box142  label="Cube116"
  AttacherType = Attacher::AttachEngine3D
  Height = 4.2
  Length = 1
  Placement = pos=(-89,19,-111.2) rot=(0,0,1;0rad)
  Width = 8
FEATURE [Part::Prism] Prism029
  AttacherType = Attacher::AttachEngine3D
  Circumradius = 3.4
  Height = 2.4
  Placement = pos=(-85,23,-110.2) rot=(0,0,1;0.523599rad)
  Polygon = 6
FEATURE [Part::Box] Box144  label="Cube118"
  AttacherType = Attacher::AttachEngine3D
  Height = 4.2
  Length = 7
  Placement = pos=(-88,19,-111.2) rot=(0,0,1;0rad)
  Width = 8
FEATURE [Part::Box] Box140  label="Cube114"
  AttacherType = Attacher::AttachEngine3D
  Height = 2.4
  Length = 24
  Placement = pos=(-85,19.6,-110.2) rot=(0,0,1;0rad)
  Width = 6.8
FEATURE [Part::Prism] Prism032
  AttacherType = Attacher::AttachEngine3D
  Circumradius = 3.4
  Height = 2.4
  Placement = pos=(-85,23,-110.2) rot=(0,0,1;0.523599rad)
  Polygon = 6
FEATURE [Part::Prism] Prism028
  AttacherType = Attacher::AttachEngine3D
  Circumradius = 3.4
  Height = 2.4
  Placement = pos=(-85,23,-110.2) rot=(0,0,1;0.523599rad)
  Polygon = 6
FEATURE [Part::MultiFuse] Fusion007002009027003005008003003006005017002002002002002002002032046
  Placement = pos=(0,0,-0.1) rot=(0,0,1;0rad)
  Shapes = -> [Prism028,Box131]
FEATURE [Part::Prism] Prism026
  AttacherType = Attacher::AttachEngine3D
  Circumradius = 3.4
  Height = 2.4
  Placement = pos=(-85,23,-110.2) rot=(0,0,1;0.523599rad)
  Polygon = 6
FEATURE [Part::MultiFuse] Fusion007002009027003005008003003006005017002002002002002002002032042
  Placement = pos=(0,0,-0.1) rot=(0,0,1;0rad)
  Shapes = -> [Prism026,Box126]
FEATURE [Part::Cut] Cut001001001002003001008002002033001001001001001001001002001001002001045002003017008007002010007002014003017120  label="pocket_v023"
  Base = -> Fusion007002009027003005008003003006005017002002002002002002002032043
  Placement = pos=(23.9,108,-212) rot=(0.57735,0.57735,0.57735;2.0944rad)
  Tool = -> Fusion007002009027003005008003003006005017002002002002002002002032042
FEATURE [Part::Box] Box129  label="Cube103"
  AttacherType = Attacher::AttachEngine3D
  Height = 2.4
  Length = 24
  Placement = pos=(-85,19.6,-110.2) rot=(0,0,1;0rad)
  Width = 6.8
FEATURE [Part::MultiFuse] Fusion007002009027003005008003003006005017002002002002002002002032044
  Placement = pos=(0,0,-0.1) rot=(0,0,1;0rad)
  Shapes = -> [Prism027,Box129]
FEATURE [Part::Box] Box138  label="Cube112"
  AttacherType = Attacher::AttachEngine3D
  Height = 2.4
  Length = 24
  Placement = pos=(-85,19.6,-110.2) rot=(0,0,1;0rad)
  Width = 6.8
FEATURE [Part::Prism] Prism030
  AttacherType = Attacher::AttachEngine3D
  Circumradius = 3.4
  Height = 2.4
  Placement = pos=(-85,23,-110.2) rot=(0,0,1;0.523599rad)
  Polygon = 6
FEATURE [Part::MultiFuse] Fusion007002009027003005008003003006005017002002002002002002002032050
  Placement = pos=(0,0,-0.1) rot=(0,0,1;0rad)
  Shapes = -> [Prism030,Box138]
FEATURE [Part::Box] Box139  label="Cube113"
  AttacherType = Attacher::AttachEngine3D
  Height = 4.2
  Length = 7
  Placement = pos=(-88,19,-111.2) rot=(0,0,1;0rad)
  Width = 8
FEATURE [Part::Cylinder] Cylinder057
  Angle = 360
  AttacherType = Attacher::AttachEngine3D
  Height = 10
  Placement = pos=(-85,23,-112) rot=(0,0,1;0rad)
  Radius = 1.85
FEATURE [Part::Cut] Cut001001001002003001008002002033001001001001001001001002001001002001045002003017008007002010007002014003017121
  Base = -> Box128
  Tool = -> Cylinder057
FEATURE [Part::Box] Box127  label="Cube101"
  AttacherType = Attacher::AttachEngine3D
  Height = 4.2
  Length = 1
  Placement = pos=(-89,19,-111.2) rot=(0,0,1;0rad)
  Width = 8
FEATURE [Part::MultiFuse] Fusion007002009027003005008003003006005017002002002002002002002032045
  Shapes = -> [Box127,Cut001001001002003001008002002033001001001001001001001002001001002001045002003017008007002010007002014003017121]
FEATURE [Part::Cut] Cut001001001002003001008002002033001001001001001001001002001001002001045002003017008007002010007002014003017122  label="pocket_v024"
  Base = -> Fusion007002009027003005008003003006005017002002002002002002002032045
  Placement = pos=(23.9,1.4e-14,-122) rot=(0.57735,-0.57735,0.57735;4.18879rad)
  Tool = -> Fusion007002009027003005008003003006005017002002002002002002002032044
FEATURE [Part::MultiFuse] Fusion007002009027003005008003003006005017002002002002002002002032061
  Shapes = -> [Cut001001001002003001008002002033001001001001001001001002001001002001045002003017008007002010007002014003017151,Cut001001001002003001008002002033001001001001001001001002001001002001045002003017008007002010007002014003017122]
FEATURE [Part::Cylinder] Cylinder059
  Angle = 360
  AttacherType = Attacher::AttachEngine3D
  Height = 10
  Placement = pos=(-85,23,-112) rot=(0,0,1;0rad)
  Radius = 1.85
FEATURE [Part::Box] Box137  label="Cube111"
  AttacherType = Attacher::AttachEngine3D
  Height = 4.2
  Length = 7
  Placement = pos=(-88,19,-111.2) rot=(0,0,1;0rad)
  Width = 8
FEATURE [Part::Cut] Cut001001001002003001008002002033001001001001001001001002001001002001045002003017008007002010007002014003017127
  Base = -> Box137
  Tool = -> Cylinder060
FEATURE [Part::Box] Box130  label="Cube104"
  AttacherType = Attacher::AttachEngine3D
  Height = 4.2
  Length = 7
  Placement = pos=(-88,19,-111.2) rot=(0,0,1;0rad)
  Width = 8
FEATURE [Part::Cut] Cut001001001002003001008002002033001001001001001001001002001001002001045002003017008007002010007002014003017123
  Base = -> Box130
  Tool = -> Cylinder058
FEATURE [Part::MultiFuse] Fusion007002009027003005008003003006005017002002002002002002002032047
  Shapes = -> [Box132,Cut001001001002003001008002002033001001001001001001001002001001002001045002003017008007002010007002014003017123]
FEATURE [Part::Cut] Cut001001001002003001008002002033001001001001001001001002001001002001045002003017008007002010007002014003017124  label="pocket_v025"
  Base = -> Fusion007002009027003005008003003006005017002002002002002002002032047
  Placement = pos=(23.9,1.4e-14,-166) rot=(0.57735,-0.57735,0.57735;4.18879rad)
  Tool = -> Fusion007002009027003005008003003006005017002002002002002002002032046
FEATURE [Part::MultiFuse] Fusion007002009027003005008003003006005017002002002002002002002032062
  Shapes = -> [Fusion007002009027003005008003003006005017002002002002002002002032061,Cut001001001002003001008002002033001001001001001001001002001001002001045002003017008007002010007002014003017124]
FEATURE [Part::Box] Box136  label="Cube110"
  AttacherType = Attacher::AttachEngine3D
  Height = 4.2
  Length = 1
  Placement = pos=(-89,19,-111.2) rot=(0,0,1;0rad)
  Width = 8
FEATURE [Part::MultiFuse] Fusion007002009027003005008003003006005017002002002002002002002032051
  Shapes = -> [Box136,Cut001001001002003001008002002033001001001001001001001002001001002001045002003017008007002010007002014003017127]
FEATURE [Part::Cut] Cut001001001002003001008002002033001001001001001001001002001001002001045002003017008007002010007002014003017128  label="pocket_v027"
  Base = -> Fusion007002009027003005008003003006005017002002002002002002002032051
  Placement = pos=(206.3,108,-212) rot=(0.57735,0.57735,0.57735;2.0944rad)
  Tool = -> Fusion007002009027003005008003003006005017002002002002002002002032050
FEATURE [Part::Box] Box134  label="Cube108"
  AttacherType = Attacher::AttachEngine3D
  Height = 4.2
  Length = 7
  Placement = pos=(-88,19,-111.2) rot=(0,0,1;0rad)
  Width = 8
FEATURE [Part::Cut] Cut001001001002003001008002002033001001001001001001001002001001002001045002003017008007002010007002014003017125
  Base = -> Box134
  Tool = -> Cylinder059
FEATURE [Part::Box] Box135  label="Cube109"
  AttacherType = Attacher::AttachEngine3D
  Height = 2.4
  Length = 24
  Placement = pos=(-85,19.6,-110.2) rot=(0,0,1;0rad)
  Width = 6.8
FEATURE [Part::MultiFuse] Fusion007002009027003005008003003006005017002002002002002002002032048
  Placement = pos=(0,0,-0.1) rot=(0,0,1;0rad)
  Shapes = -> [Prism029,Box135]
FEATURE [Part::Prism] Prism031
  AttacherType = Attacher::AttachEngine3D
  Circumradius = 3.4
  Height = 2.4
  Placement = pos=(-85,23,-110.2) rot=(0,0,1;0.523599rad)
  Polygon = 6
FEATURE [Part::MultiFuse] Fusion007002009027003005008003003006005017002002002002002002002032052
  Placement = pos=(0,0,-0.1) rot=(0,0,1;0rad)
  Shapes = -> [Prism031,Box140]
FEATURE [Part::Box] Box133  label="Cube107"
  AttacherType = Attacher::AttachEngine3D
  Height = 4.2
  Length = 1
  Placement = pos=(-89,19,-111.2) rot=(0,0,1;0rad)
  Width = 8
FEATURE [Part::MultiFuse] Fusion007002009027003005008003003006005017002002002002002002002032049
  Shapes = -> [Box133,Cut001001001002003001008002002033001001001001001001001002001001002001045002003017008007002010007002014003017125]
FEATURE [Part::Cut] Cut001001001002003001008002002033001001001001001001001002001001002001045002003017008007002010007002014003017126  label="pocket_v026"
  Base = -> Fusion007002009027003005008003003006005017002002002002002002002032049
  Placement = pos=(206.3,108,-168) rot=(0.57735,0.57735,0.57735;2.0944rad)
  Tool = -> Fusion007002009027003005008003003006005017002002002002002002002032048
FEATURE [Part::Cylinder] Cylinder061
  Angle = 360
  AttacherType = Attacher::AttachEngine3D
  Height = 10
  Placement = pos=(-85,23,-112) rot=(0,0,1;0rad)
  Radius = 1.85
FEATURE [Part::Cut] Cut001001001002003001008002002033001001001001001001001002001001002001045002003017008007002010007002014003017129
  Base = -> Box139
  Tool = -> Cylinder061
FEATURE [Part::Box] Box141  label="Cube115"
  AttacherType = Attacher::AttachEngine3D
  Height = 4.2
  Length = 1
  Placement = pos=(-89,19,-111.2) rot=(0,0,1;0rad)
  Width = 8
FEATURE [Part::MultiFuse] Fusion007002009027003005008003003006005017002002002002002002002032053
  Shapes = -> [Box141,Cut001001001002003001008002002033001001001001001001001002001001002001045002003017008007002010007002014003017129]
FEATURE [Part::Cut] Cut001001001002003001008002002033001001001001001001001002001001002001045002003017008007002010007002014003017130  label="pocket_v028"
  Base = -> Fusion007002009027003005008003003006005017002002002002002002002032053
  Placement = pos=(206.3,1.4e-14,-122) rot=(0.57735,-0.57735,0.57735;4.18879rad)
  Tool = -> Fusion007002009027003005008003003006005017002002002002002002002032052
FEATURE [Part::MultiFuse] Fusion007002009027003005008003003006005017002002002002002002002032063
  Shapes = -> [Fusion007002009027003005008003003006005017002002002002002002002032062,Cut001001001002003001008002002033001001001001001001001002001001002001045002003017008007002010007002014003017130]
FEATURE [Part::Cylinder] Cylinder062
  Angle = 360
  AttacherType = Attacher::AttachEngine3D
  Height = 10
  Placement = pos=(-85,23,-112) rot=(0,0,1;0rad)
  Radius = 1.85
FEATURE [Part::Cut] Cut001001001002003001008002002033001001001001001001001002001001002001045002003017008007002010007002014003017131
  Base = -> Box144
  Tool = -> Cylinder062
FEATURE [Part::MultiFuse] Fusion007002009027003005008003003006005017002002002002002002002032054
  Shapes = -> [Box142,Cut001001001002003001008002002033001001001001001001001002001001002001045002003017008007002010007002014003017131]
FEATURE [Part::Box] Box143  label="Cube117"
  AttacherType = Attacher::AttachEngine3D
  Height = 2.4
  Length = 24
  Placement = pos=(-85,19.6,-110.2) rot=(0,0,1;0rad)
  Width = 6.8
FEATURE [Part::MultiFuse] Fusion007002009027003005008003003006005017002002002002002002002032055
  Placement = pos=(0,0,-0.1) rot=(0,0,1;0rad)
  Shapes = -> [Prism032,Box143]
FEATURE [Part::Cut] Cut001001001002003001008002002033001001001001001001001002001001002001045002003017008007002010007002014003017132  label="pocket_v029"
  Base = -> Fusion007002009027003005008003003006005017002002002002002002002032054
  Placement = pos=(206.3,1.4e-14,-166) rot=(0.57735,-0.57735,0.57735;4.18879rad)
  Tool = -> Fusion007002009027003005008003003006005017002002002002002002002032055
FEATURE [Part::MultiFuse] Fusion007002009027003005008003003006005017002002002002002002002032064
  Shapes = -> [Fusion007002009027003005008003003006005017002002002002002002002032063,Cut001001001002003001008002002033001001001001001001001002001001002001045002003017008007002010007002014003017132]
FEATURE [Part::Cut] Cut001001001002003001008002002033001001001001001001001002001001002001045002003017008007002010007002014003017154
  Base = -> Fusion007002009027003005008003003006005017002002002002002002002032064
  Tool = -> Box153
FEATURE [Part::MultiFuse] Fusion007002009027003005008003003006005017002002002002002002002032065  label="tapa_enrejillada_v3"
  Shapes = -> [Cut001001001002003001008002002033001001001001001001001002001001002001045002003017008007002010007002014003017154,Cut001001001002003001008002002033001001001001001001001002001001002001045002003017008007002010007002014003017144]
FEATURE [Part::Box] Box145  label="base_tapa"
  AttacherType = Attacher::AttachEngine3D
  Height = 119.6
  Length = 186.6
  Placement = pos=(-87.3,21,-226.8) rot=(0,0,1;0rad)
  Width = 1.5
FEATURE [Part::Cut] Cut001001001002003001008002002033001001001001001001001002001001002001045002003017008007002010007002014003017133
  Base = -> Box145
  Tool = -> Box146
FEATURE [Part::Cut] Cut001001001002003001008002002033001001001001001001001002001001002001045002003017008007002010007002014003017134
  Base = -> Cut001001001002003001008002002033001001001001001001001002001001002001045002003017008007002010007002014003017133
  Tool = -> Box149
FEATURE [Part::Cut] Cut001001001002003001008002002033001001001001001001001002001001002001045002003017008007002010007002014003017135
  Base = -> Cut001001001002003001008002002033001001001001001001001002001001002001045002003017008007002010007002014003017134
  Tool = -> Box148
FEATURE [Part::Cut] Cut001001001002003001008002002033001001001001001001001002001001002001045002003017008007002010007002014003017136  label="base_tapa_1"
  Base = -> Cut001001001002003001008002002033001001001001001001001002001001002001045002003017008007002010007002014003017135
  Placement = pos=(0,-2,0) rot=(0,0,1;0rad)
  Tool = -> Box147
FEATURE [Part::MultiFuse] Fusion007002009027003005008003003006005017002002002002002002002032056
  Shapes = -> [Cut001001001002003001008002002033001001001001001001001002001001002001045002003017008007002010007002014003017136,Cut001001001002003001008002002033001001001001001001001002001001002001045002003017008007002010007002014003017128]
FEATURE [Part::MultiFuse] Fusion007002009027003005008003003006005017002002002002002002002032057
  Shapes = -> [Fusion007002009027003005008003003006005017002002002002002002002032056,Cut001001001002003001008002002033001001001001001001001002001001002001045002003017008007002010007002014003017126]
FEATURE [Part::MultiFuse] Fusion007002009027003005008003003006005017002002002002002002002032058
  Shapes = -> [Fusion007002009027003005008003003006005017002002002002002002002032057,Cut001001001002003001008002002033001001001001001001001002001001002001045002003017008007002010007002014003017120]
FEATURE [Part::MultiFuse] Fusion007002009027003005008003003006005017002002002002002002002032059  label="base_base_11_sin_panal"
  Shapes = -> [Fusion007002009027003005008003003006005017002002002002002002002032058,Cut001001001002003001008002002033001001001001001001001002001001002001045002003017008007002010007002014003017117]
FEATURE [Part::Cut] Cut001001001002003001008002002033001001001001001001001002001001002001045002003017008007002010007002014003017145  label="base_enrejillada_v3_sin_panal"
  Base = -> Fusion007002009027003005008003003006005017002002002002002002002032059
  Tool = -> Box150
FEATURE [Part::MultiFuse] Fusion007002009027003005008003003006005017002002002002002002002032066  label="base_enrejillada_v3"
  Shapes = -> [Cut001001001002003001008002002033001001001001001001001002001001002001045002003017008007002010007002014003017145,Cut001001001002003001008002002033001001001001001001001002001001002001045002003017008007002010007002014003017155]
